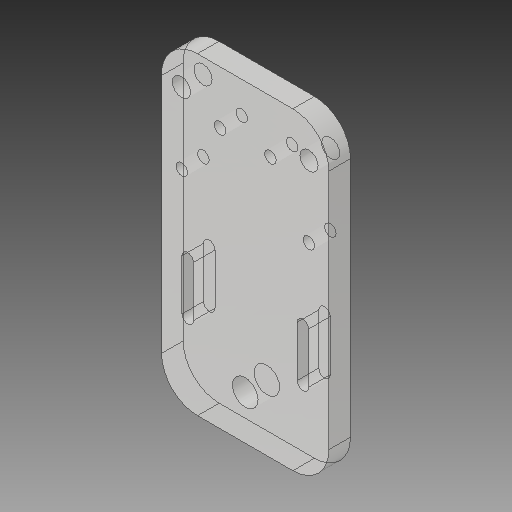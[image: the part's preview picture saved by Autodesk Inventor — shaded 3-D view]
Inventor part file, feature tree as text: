
AUTODESK INVENTOR PART (.ipt)
format: ipt  version: 2017 (Build 210142000, 142)  size: 181,760 bytes
history: native  units: mm
features: other x3, sketch x2
ambient origin geometry x8: Origin, YZ Plane, XZ Plane, XY Plane, X Axis, Y Axis, Z Axis, Center Point
bodies: Solid1 (feature_tree)
feature tree (5):
  other  "Hotend Front Plate revised.ipt"
  other  "Solid1::Hotend Front Plate revised.ipt"
  other  "TaggingFeature1"
  sketch  "Sketch1"  dims[d0=10.0mm]
  sketch  "Sketch2"
